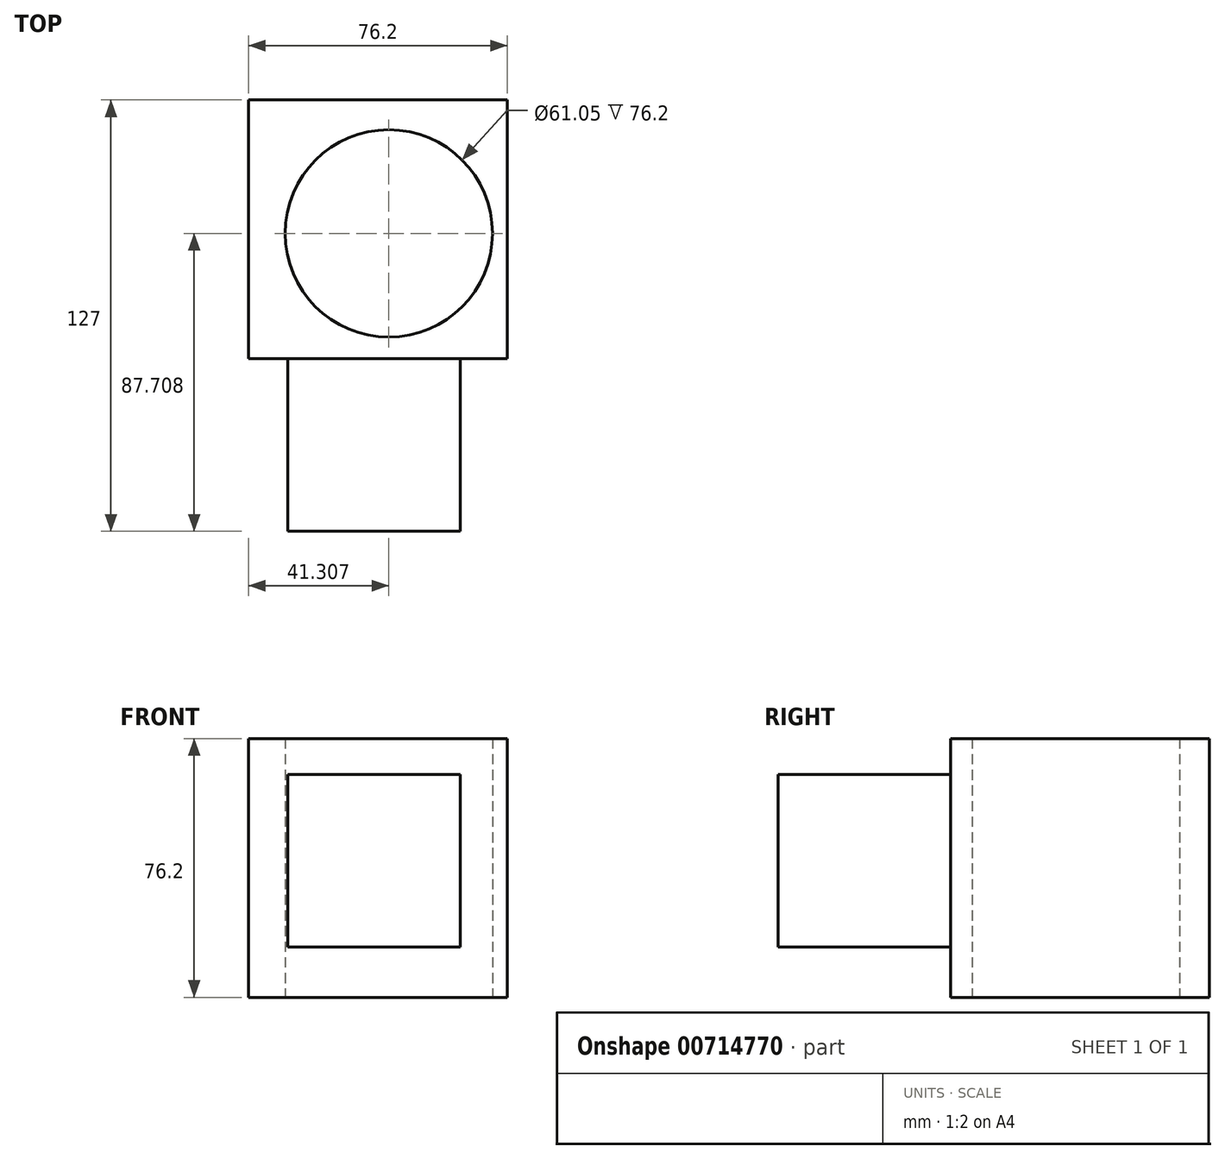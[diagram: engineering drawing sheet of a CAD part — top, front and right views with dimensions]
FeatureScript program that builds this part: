
annotation { "Feature Type Name" : "Feature", "Feature Type Description" : "" }
export const myFeature = defineFeature(function(context is Context, id is Id, definition is map)
    precondition{}
    {
        {
            var Q0;
            Q0=qCreatedBy(makeId("Front.planeOp"),FACE);
            var sketch = newSketch(context, id + "F0", { "sketchPlane" : qUnion([Q0])});
            skLineSegment(sketch, "E0.bottom", {"start": v(-37.98, 35.89) * mm, "end": v(38.22, 35.89) * mm});
            skLineSegment(sketch, "E0.top", {"start": v(-37.98, -40.31) * mm, "end": v(38.22, -40.31) * mm});
            skLineSegment(sketch, "E0.left", {"start": v(-37.98, 35.89) * mm, "end": v(-37.98, -40.31) * mm});
            skLineSegment(sketch, "E0.right", {"start": v(38.22, 35.89) * mm, "end": v(38.22, -40.31) * mm});
            skSolve(sketch);
        }
        {
            var Q0;
            Q0=makeQuery(id+"F0.imprint","IMPRINT",FACE,{"disambiguationData":[TD([[makeQuery(id+"F0.imprint","IMPRINT",EDGE,{"derivedFrom":sQuery(id+"F0.wireOp",EDGE,"E0.bottom")}),-1.0]])]});
            extrude(context, id + "F1", {"entities" : qUnion([Q0]), "depth" : 76.2 * mm, "offsetDistance" : 25.4 * mm});
        }
        {
            var Q0;
            Q0=makeQuery(id+"F1.opExtrude","CAP_FACE",FACE,{"disambiguationData":[OSD([sQuery(id+"F0.wireOp",EDGE,"E0.bottom"),sQuery(id+"F0.wireOp",EDGE,"E0.top"),sQuery(id+"F0.wireOp",EDGE,"E0.left"),sQuery(id+"F0.wireOp",EDGE,"E0.right")])],"isStart":false});
            var sketch = newSketch(context, id + "F2", { "sketchPlane" : qUnion([Q0])});
            skLineSegment(sketch, "E1.bottom", {"start": v(-26.37, 25.34) * mm, "end": v(24.43, 25.34) * mm});
            skLineSegment(sketch, "E1.top", {"start": v(-26.37, -25.46) * mm, "end": v(24.43, -25.46) * mm});
            skLineSegment(sketch, "E1.left", {"start": v(-26.37, 25.34) * mm, "end": v(-26.37, -25.46) * mm});
            skLineSegment(sketch, "E1.right", {"start": v(24.43, 25.34) * mm, "end": v(24.43, -25.46) * mm});
            skSolve(sketch);
        }
        {
            var Q0;
            Q0=makeQuery(id+"F2.imprint","IMPRINT",FACE,{"disambiguationData":[TD([[makeQuery(id+"F2.imprint","IMPRINT",EDGE,{"derivedFrom":sQuery(id+"F2.wireOp",EDGE,"E1.bottom")}),-1.0]])]});
            extrude(context, id + "F3", {"entities" : qUnion([Q0]), "operationType" : NewBodyOperationType.ADD, "depth" : 50.8 * mm, "offsetDistance" : 25.4 * mm});
        }
        {
            var Q0;
            Q0=makeQuery(id+"F1.opExtrude","SWEPT_FACE",FACE,{"disambiguationData":[OSD([sQuery(id+"F0.wireOp",EDGE,"E0.top")])]});
            var sketch = newSketch(context, id + "F4", { "sketchPlane" : qUnion([Q0])});
            skCircle(sketch, "E2", {"center": v(3.33, 39.3) * mm, "radius": 30.52 * mm});
            skSolve(sketch);
        }
        {
            var Q0;
            Q0=makeQuery(id+"F4.imprint","IMPRINT",FACE,{"disambiguationData":[TD([[makeQuery(id+"F4.imprint","IMPRINT",EDGE,{"derivedFrom":sQuery(id+"F4.wireOp",EDGE,"E2")}),1.0]])]});
            extrude(context, id + "F5", {"entities" : qUnion([Q0]), "operationType" : NewBodyOperationType.REMOVE, "oppositeDirection" : true, "depth" : 101.6 * mm, "offsetDistance" : 25.4 * mm});
        }
    });
